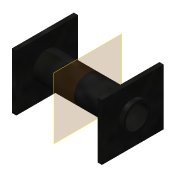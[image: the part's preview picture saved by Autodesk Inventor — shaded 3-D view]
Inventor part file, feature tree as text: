
AUTODESK INVENTOR PART (.ipt)
format: ipt  version: 2018.1 (Build 221171000, 171)  size: 114,688 bytes
history: native  units: mm
features: other x3, extrude x2, sketch x2, mirror x1
ambient origin geometry x8: Origin, YZ Plane, XZ Plane, XY Plane, X Axis, Y Axis, Z Axis, Center Point
bodies: Body1 (feature_tree)
feature tree (8):
  other  "frame"
  other  "Твердое тело1"
  extrude  "Выдавливание1"  Depth=22.0mm
  other  "РабПлоскость1"
  mirror  "Зеркальное отражение1"
  extrude  "Выдавливание2"  Depth=20.0mm
  sketch  "Эскиз1"
  sketch  "Эскиз2"
